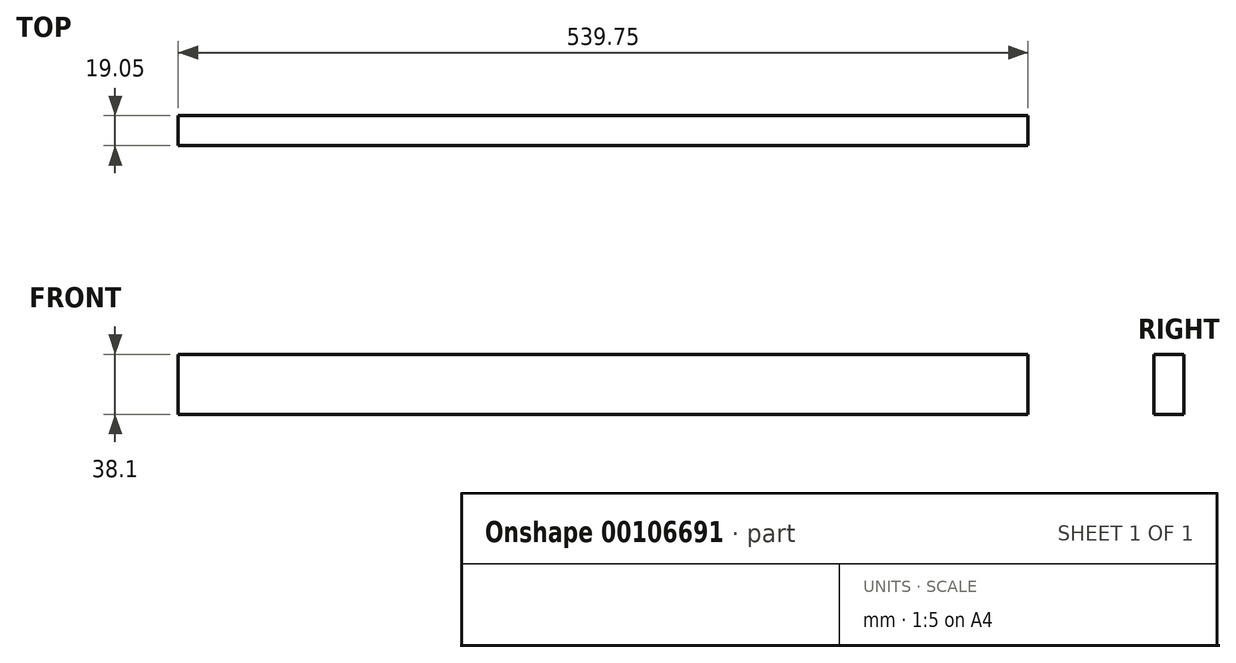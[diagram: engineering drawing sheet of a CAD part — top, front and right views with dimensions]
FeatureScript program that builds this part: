
annotation { "Feature Type Name" : "Feature", "Feature Type Description" : "" }
export const myFeature = defineFeature(function(context is Context, id is Id, definition is map)
    precondition{}
    {
        {
            var Q0;
            Q0=qCreatedBy(makeId("Front.planeOp"),FACE);
            var sketch = newSketch(context, id + "F0", { "sketchPlane" : qUnion([Q0])});
            skLineSegment(sketch, "E0.bottom", {"start": v(0, 0) * mm, "end": v(539.75, 0) * mm});
            skLineSegment(sketch, "E0.top", {"start": v(0, 38.1) * mm, "end": v(539.75, 38.1) * mm});
            skLineSegment(sketch, "E0.left", {"start": v(0, 0) * mm, "end": v(0, 38.1) * mm});
            skLineSegment(sketch, "E0.right", {"start": v(539.75, 0) * mm, "end": v(539.75, 38.1) * mm});
            skSolve(sketch);
        }
        {
            var Q0;
            Q0=makeQuery(id+"F0.imprint","IMPRINT",FACE,{"disambiguationData":[TD([[makeQuery(id+"F0.imprint","IMPRINT",EDGE,{"derivedFrom":sQuery(id+"F0.wireOp",EDGE,"E0.bottom")}),1.0]])]});
            extrude(context, id + "F1", {"entities" : qUnion([Q0]), "depth" : 19.05 * mm});
        }
    });
